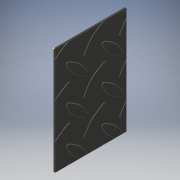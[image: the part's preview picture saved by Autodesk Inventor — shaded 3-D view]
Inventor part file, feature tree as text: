
AUTODESK INVENTOR PART (.ipt)
format: ipt  version: 2016 (Build 200138000, 138)  size: 114,176 bytes
history: native  units: in
note: dims shown in document units (in); Inventor stores cm internally (conversion verified against a paired STEP export)
features: sketch x2, extrude x1
ambient origin geometry x8: Origin, YZ Plane, XZ Plane, XY Plane, X Axis, Y Axis, Z Axis, Center Point
bodies: Solid1 (feature_tree)
feature tree (3):
  sketch  "Sketch1"  dims[d0=3.33in d1=5.0in]
  extrude  "Extrusion1"  Depth=5.0in
  sketch  "Sketch2"  dims[d2=0.071in d3=0.0in]
